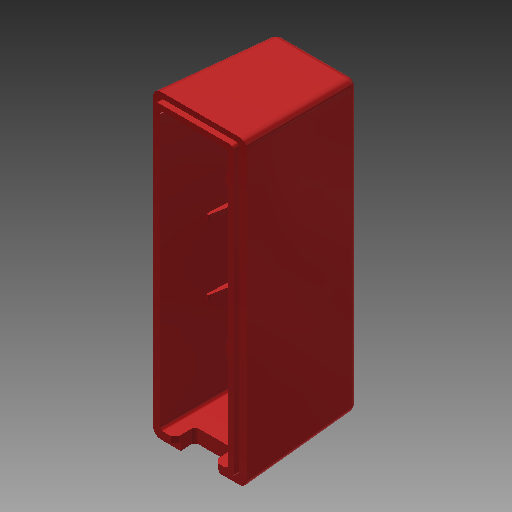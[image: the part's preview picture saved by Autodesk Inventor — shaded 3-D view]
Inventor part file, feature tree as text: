
AUTODESK INVENTOR PART (.ipt)
format: ipt  version: 2018 (Build 220112000, 112)  size: 386,048 bytes
history: native  units: in
note: dims shown in document units (in); Inventor stores cm internally (conversion verified against a paired STEP export)
features: sketch x11, plane x9, extrude x8, projected_geometry x6, fillet x5, other x2, mirror x2, thread x2, reference x2, hole x1, loft x1, pattern_linear x1, chamfer x1
ambient origin geometry x8: Origin, YZ Plane, XZ Plane, XY Plane, X Axis, Y Axis, Z Axis, Center Point
bodies: Solid1 (feature_tree)
feature tree (51):
  extrude  "Extrusion1"  Depth=0.028in
  fillet  "Fillet1"  Radius=0.028in
  sketch  "Sketch2"  dims[d6=0.04in d7=0.04in]
  extrude  "Extrusion3"  Depth=0.04in
  extrude  "Extrusion4"  Depth=0.028in
  fillet  "Fillet4"  Radius=0.028in
  fillet  "Fillet6"  Radius=0.539in
  plane  "Work Plane1"
  extrude  "Extrusion5"  Depth=0.02in
  hole  "Hole1"  [1 undecoded]
  plane  "Work Plane2"
  extrude  "Extrusion6"  Depth=0.5625in TaperAngle=0.0deg
  other  "Work Axis1"
  other  "Work Axis2"
  plane  "Work Plane4"
  mirror  "Mirror1"
  fillet  "Fillet7"  Radius=0.197in
  loft  "Loft1"
  plane  "Work Plane6"
  extrude  "Extrusion9"  Depth=0.374in TaperAngle=0.0deg
  extrude  "Extrusion10"  Depth=0.26in
  fillet  "Fillet9"  Radius=0.528in
  pattern_linear  "Rectangular Pattern1"  Spacing1=0.0in  [1 undecoded]
  plane  "Work Plane7"
  mirror  "Mirror2"
  plane  "Work Plane8"
  plane  "Work Plane9"
  extrude  "Extrusion12"  TaperAngle=0.0deg  [1 undecoded]
  chamfer  "Chamfer3"  [1 undecoded]
  thread  "Thread1"  [1 undecoded]
  thread  "Thread2"  [1 undecoded]
  sketch  "Sketch1"  dims[d0=0.598in d1=-0.0206in d2=0.039in d3=0.028in]
  projected_geometry  "Projected Loop1"
  sketch  "Sketch3"  dims[d8=0.04in d9=0.028in d10=0.028in d11=0.0in d14=0.539in d15=-0.0206in]
  sketch  "Sketch4"  dims[d16=0.059in d18=0.02in]
  reference  "Reference1"
  reference  "Reference2"
  sketch  "Sketch5"  dims[d19=0.479in d20=0.303in]
  projected_geometry  "Projected Loop2"
  sketch  "Sketch7"  dims[d21=0.157in d22=0.5625in d23=0.0in]
  projected_geometry  "Projected Loop4"
  projected_geometry  "Projected Loop5"
  plane  "Work Plane3"
  sketch  "Sketch10"  dims[d24=0.067in d25=0.75in d26=0.375in d27=0.25in d28=0.5635in d29=0.323in d30=0.0in d31=0.197in]
  sketch  "Sketch11"  dims[d32=0.073in d33=0.033in]
  projected_geometry  "Projected Loop8"
  plane  "Work Plane5"
  sketch  "Sketch13"  dims[d34=1.0in d35=0.0069in d36=0.0in d37=0.374in]
  sketch  "Sketch14"  dims[d43=0.02in d44=0.26in d45=0.528in]
  sketch  "Sketch16"  dims[d47=0.26in d48=0.0in d49=90.0deg d50=0.0in d51=90.0deg d63=-0.064in d64=0.316in d65=0.028in d66=0.0in d67=0.02in d68=0.112in d69=0.028in d70=0.0in d71=0.0155in d72=0.01in d73=0.7874in d75=0.354in d76=0.0in d88=0.0in d89=0.0197in d90=0.197in d91=0.099in d92=0.028in d93=0.0in d94=0.02in d95=0.112in d96=45.0deg d97=1.0in d98=0.0in d99=1.0in d100=0.0in]
  projected_geometry  "Projected Loop10"
note: 6 required parameter values undecoded (feature->parameter linkage not recoverable at this tier; creation-order binding heuristic only, values carry confidence <= 0.55)
